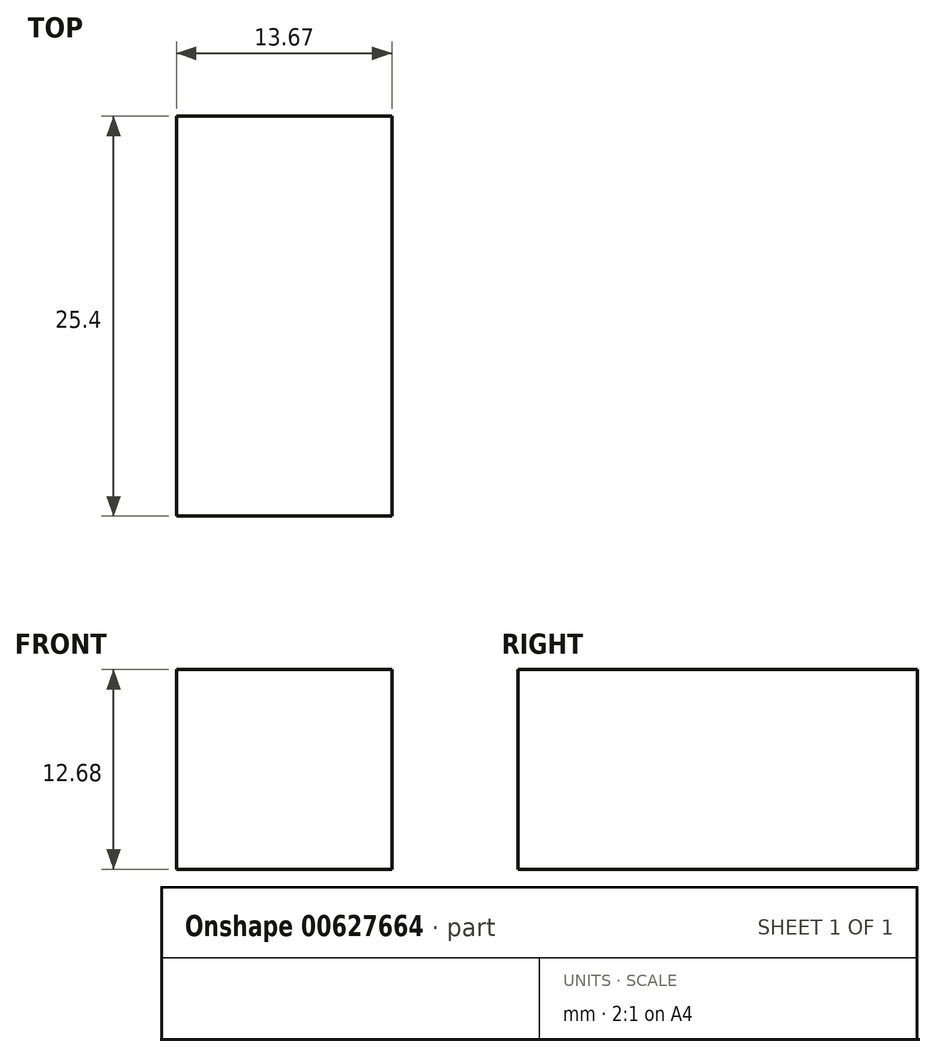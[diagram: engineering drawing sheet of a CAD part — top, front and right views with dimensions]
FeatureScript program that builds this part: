
annotation { "Feature Type Name" : "Feature", "Feature Type Description" : "" }
export const myFeature = defineFeature(function(context is Context, id is Id, definition is map)
    precondition{}
    {
        {
            var Q0;
            Q0=qCreatedBy(makeId("Front.planeOp"),FACE);
            var sketch = newSketch(context, id + "F0", { "sketchPlane" : qUnion([Q0])});
            skLineSegment(sketch, "E0.bottom", {"start": v(0, 0) * mm, "end": v(-30.84, 0) * mm});
            skLineSegment(sketch, "E0.top", {"start": v(0, 25.61) * mm, "end": v(-30.84, 25.61) * mm});
            skLineSegment(sketch, "E0.left", {"start": v(0, 0) * mm, "end": v(0, 25.61) * mm});
            skLineSegment(sketch, "E0.right", {"start": v(-30.84, 0) * mm, "end": v(-30.84, 25.61) * mm});
            skLineSegment(sketch, "E1.top", {"start": v(0, 12.68) * mm, "end": v(-13.67, 12.68) * mm});
            skLineSegment(sketch, "E1.left", {"start": v(0, 0) * mm, "end": v(0, 12.68) * mm});
            skLineSegment(sketch, "E1.right", {"start": v(-13.67, 0) * mm, "end": v(-13.67, 12.68) * mm});
            skSolve(sketch);
        }
        {
            var Q0;
            Q0=makeQuery(id+"F0.imprint","IMPRINT",FACE,{"disambiguationData":[TD([[makeQuery(id+"F0.imprint","IMPRINT",EDGE,{"derivedFrom":sQuery(id+"F0.wireOp",EDGE,"E0.bottom")}),-1.0]])]});
            extrude(context, id + "F1", {"entities" : qUnion([Q0]), "depth" : 25.4 * mm, "offsetDistance" : 25.4 * mm});
        }
    });
